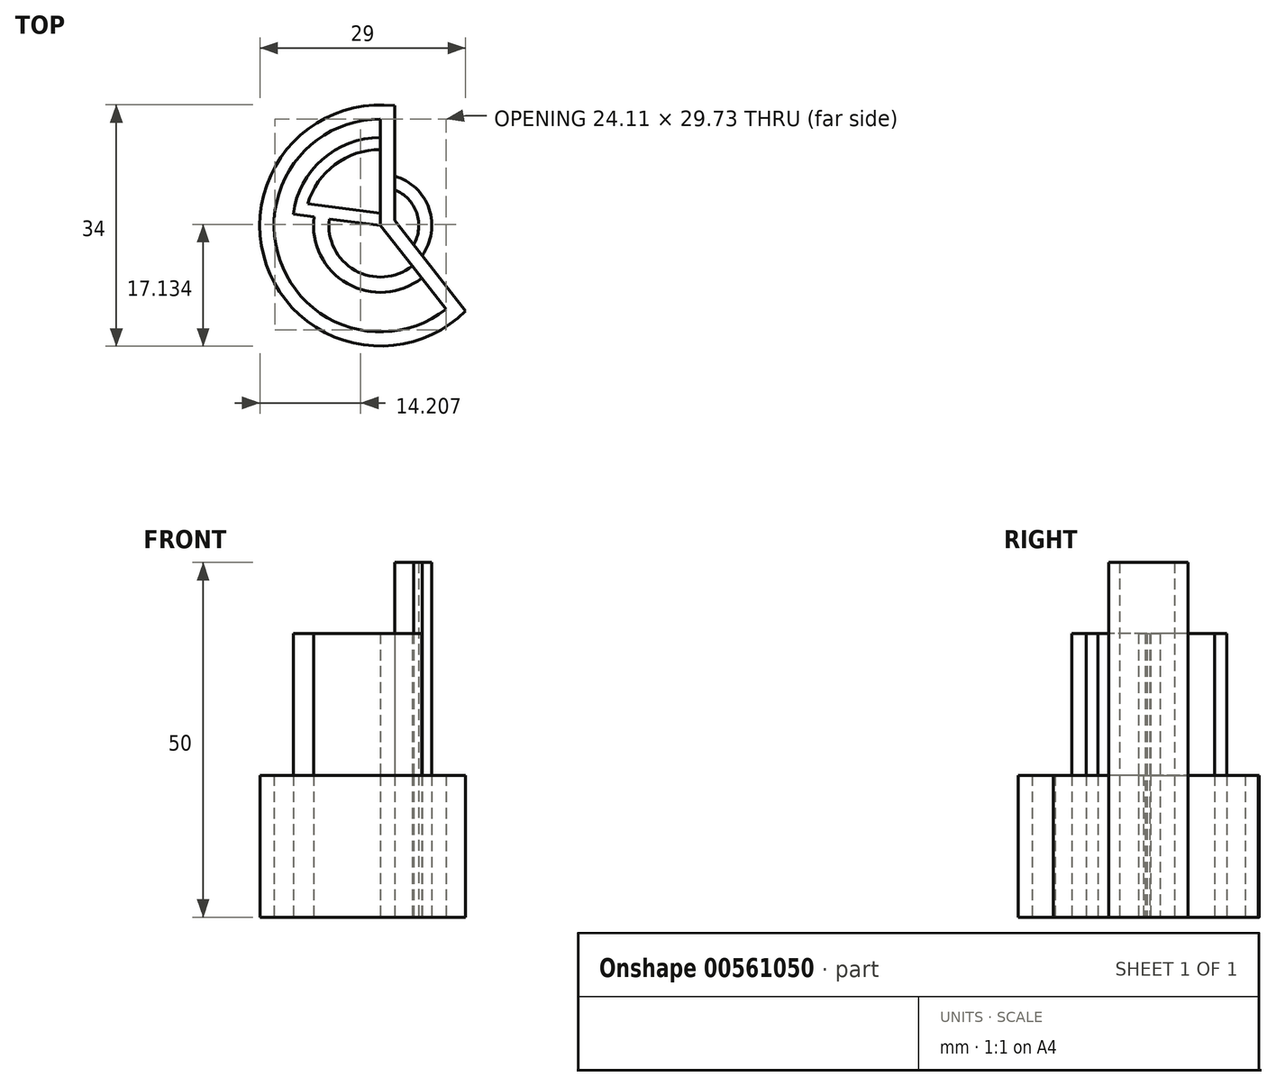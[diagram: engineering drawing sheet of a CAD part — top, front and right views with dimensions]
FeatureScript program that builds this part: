
annotation { "Feature Type Name" : "Feature", "Feature Type Description" : "" }
export const myFeature = defineFeature(function(context is Context, id is Id, definition is map)
    precondition{}
    {
        {
            var Q0;
            Q0=qCreatedBy(makeId("Top.planeOp"),FACE);
            var sketch = newSketch(context, id + "F0", { "sketchPlane" : qUnion([Q0])});
            skLineSegment(sketch, "E0.bottom", {"start": v(-15, 15) * mm, "end": v(15, 15) * mm, "construction": true});
            skLineSegment(sketch, "E0.top", {"start": v(-15, -15) * mm, "end": v(15, -15) * mm, "construction": true});
            skLineSegment(sketch, "E0.left", {"start": v(-15, 15) * mm, "end": v(-15, -15) * mm});
            skLineSegment(sketch, "E0.right", {"start": v(15, 15) * mm, "end": v(15, -15) * mm, "construction": true});
            skArc(sketch, "E1", {"start": v(0, 15) * mm, "mid": v(-14.18, -4.9) * mm, "end": v(9.26, -11.8) * mm});
            skLineSegment(sketch, "E2", {"start": v(0, 0) * mm, "end": v(0, 15) * mm});
            skLineSegment(sketch, "E3", {"start": v(0, 0) * mm, "end": v(9.26, -11.8) * mm});
            skLineSegment(sketch, "E4.0", {"start": v(2, 0.7) * mm, "end": v(2, 16.88) * mm});
            skLineSegment(sketch, "E4.1", {"start": v(2, 0.7) * mm, "end": v(12, -12.05) * mm});
            skArc(sketch, "E4.2", {"start": v(2, 16.88) * mm, "mid": v(-16.07, -5.55) * mm, "end": v(12, -12.05) * mm});
            skSolve(sketch);
        }
        {
            var Q0;
            Q0 = qSketchRegion(id + "F0", true);
            extrude(context, id + "F1", {"entities" : qUnion([Q0]), "depth" : 20 * mm, "offsetDistance" : 25 * mm});
        }
        {
            var Q0;
            Q0=qCreatedBy(makeId("Top.planeOp"),FACE);
            var sketch = newSketch(context, id + "F2", { "sketchPlane" : qUnion([Q0])});
            skArc(sketch, "E5.0", {"start": v(0, 15) * mm, "mid": v(-14.18, -4.9) * mm, "end": v(9.26, -11.8) * mm});
            skLineSegment(sketch, "E6", {"start": v(0, 0) * mm, "end": v(-12.3, 1.58) * mm});
            skArc(sketch, "E7.0", {"start": v(0, 12.4) * mm, "mid": v(-8.19, 9.31) * mm, "end": v(-12.3, 1.58) * mm});
            skLineSegment(sketch, "E8.0", {"start": v(0, 1.71) * mm, "end": v(-10.26, 3.04) * mm});
            skArc(sketch, "E8.1", {"start": v(0, 10.7) * mm, "mid": v(-6.4, 8.57) * mm, "end": v(-10.26, 3.04) * mm});
            skLineSegment(sketch, "E9.0", {"start": v(0, 0) * mm, "end": v(0, 1.71) * mm});
            skLineSegment(sketch, "E10.trimOffspring", {"start": v(0, 10.7) * mm, "end": v(0, 12.4) * mm});
            skSolve(sketch);
        }
        {
            var Q0;
            Q0 = qSketchRegion(id + "F2", true);
            extrude(context, id + "F3", {"entities" : qUnion([Q0]), "operationType" : NewBodyOperationType.ADD, "depth" : 25 * mm, "offsetDistance" : 25 * mm});
        }
        {
            var Q0;
            Q0=qCreatedBy(makeId("Top.planeOp"),FACE);
            var sketch = newSketch(context, id + "F4", { "sketchPlane" : qUnion([Q0])});
            skArc(sketch, "E11", {"start": v(5.88, -4.25) * mm, "mid": v(6.85, 2.37) * mm, "end": v(2, 6.97) * mm});
            skArc(sketch, "E12", {"start": v(4.67, -2.71) * mm, "mid": v(5.1, 1.77) * mm, "end": v(2, 5.02) * mm});
            skLineSegment(sketch, "E13.0", {"start": v(2, 5.02) * mm, "end": v(2, 6.97) * mm});
            skLineSegment(sketch, "E14.0", {"start": v(4.67, -2.71) * mm, "end": v(5.88, -4.25) * mm});
            skPoint(sketch, "E15.orphan", {"position": v(2, 0.7) * mm});
            skPoint(sketch, "E16.orphan", {"position": v(12, -12.05) * mm});
            skPoint(sketch, "E17.orphan", {"position": v(2, 16.88) * mm});
            skSolve(sketch);
        }
        {
            var Q0;
            Q0 = qSketchRegion(id + "F4", true);
            extrude(context, id + "F5", {"entities" : qUnion([Q0]), "operationType" : NewBodyOperationType.ADD, "depth" : 50 * mm, "offsetDistance" : 25 * mm});
        }
        {
            var Q0;
            Q0=qCreatedBy(makeId("Top.planeOp"),FACE);
            var sketch = newSketch(context, id + "F6", { "sketchPlane" : qUnion([Q0])});
            skCircle(sketch, "E18", {"center": v(0, 0) * mm, "radius": 9.43 * mm});
            skCircle(sketch, "E19", {"center": v(0, 0) * mm, "radius": 7.26 * mm});
            skLineSegment(sketch, "E20.0", {"start": v(0, 0) * mm, "end": v(-12.3, 1.58) * mm});
            skLineSegment(sketch, "E21.0", {"start": v(0, 0) * mm, "end": v(5.82, -7.42) * mm});
            skLineSegment(sketch, "E22.0.2", {"start": v(2, 6.97) * mm, "end": v(2, 6.98) * mm});
            skLineSegment(sketch, "E22.0.4", {"start": v(5.88, -4.26) * mm, "end": v(5.88, -4.25) * mm});
            skPoint(sketch, "E23.orphan", {"position": v(9.26, -11.8) * mm});
            skPoint(sketch, "E24.orphan", {"position": v(12, -12.05) * mm});
            skPoint(sketch, "E25.0.0.start.orphan", {"position": v(2, 0.7) * mm});
            skPoint(sketch, "E22.0.1.start.orphan", {"position": v(2, 5.02) * mm});
            skPoint(sketch, "E25.0.5.end.orphan", {"position": v(4.67, -2.71) * mm});
            skPoint(sketch, "E26.trimOffspring.end.orphan", {"position": v(2, 16.88) * mm});
            skSolve(sketch);
        }
        {
            var Q0;
            Q0 = qSketchRegion(id + "F2", true);
            var Q1;
            {var subQ0=sQuery(id+"F6.wireOp",EDGE,"E21.0");var subQ1=sQuery(id+"F6.wireOp",EDGE,"E18");var subQ2=makeQuery(id+"F6.imprint","INTERSECT",VERTEX,{"derivedFrom":[subQ1,subQ0]});Q1=makeQuery(id+"F6.imprint","IMPRINT",FACE,{"disambiguationData":[TD([[makeQuery(id+"F6.imprint","IMPRINT",EDGE,{"disambiguationData":[TD([[subQ2,1.0]])],"derivedFrom":subQ1}),1.0]])]});}
            extrude(context, id + "F7", {"entities" : qUnion([Q0, Q1]), "operationType" : NewBodyOperationType.ADD, "depth" : 40 * mm, "offsetDistance" : 25 * mm});
        }
    });
